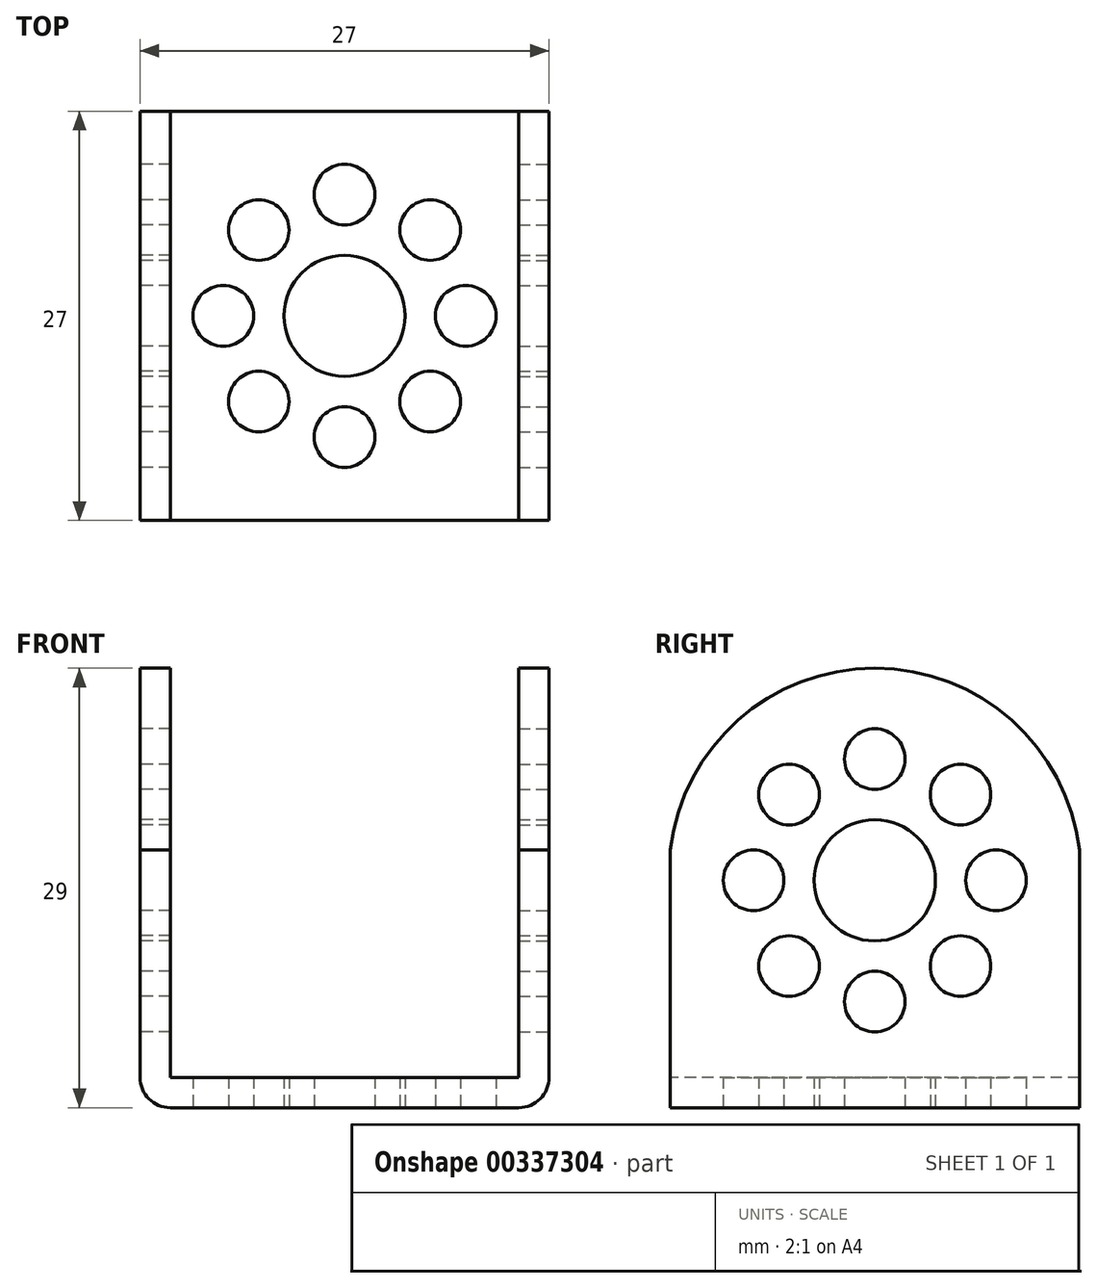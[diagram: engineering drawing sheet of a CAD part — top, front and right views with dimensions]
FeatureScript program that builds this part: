
annotation { "Feature Type Name" : "Feature", "Feature Type Description" : "" }
export const myFeature = defineFeature(function(context is Context, id is Id, definition is map)
    precondition{}
    {
        {
            var Q0;
            Q0=qCreatedBy(makeId("Top.planeOp"),FACE);
            var sketch = newSketch(context, id + "F0", { "sketchPlane" : qUnion([Q0])});
            skLineSegment(sketch, "E0.bottom", {"start": v(13.5, 13.5) * mm, "end": v(-13.5, 13.5) * mm});
            skLineSegment(sketch, "E0.top", {"start": v(13.5, -13.5) * mm, "end": v(-13.5, -13.5) * mm});
            skLineSegment(sketch, "E0.left", {"start": v(13.5, 13.5) * mm, "end": v(13.5, -13.5) * mm});
            skLineSegment(sketch, "E0.right", {"start": v(-13.5, 13.5) * mm, "end": v(-13.5, -13.5) * mm});
            skPoint(sketch, "E0.middle", {"position": v(0, 0) * mm});
            skLineSegment(sketch, "E1", {"start": v(0, 2.64) * mm, "end": v(0, 0) * mm});
            skLineSegment(sketch, "E2", {"start": v(0, 0) * mm, "end": v(0, -2.64) * mm});
            skLineSegment(sketch, "E3", {"start": v(-1.85, 0) * mm, "end": v(0, 0) * mm});
            skLineSegment(sketch, "E4", {"start": v(3.72, 0) * mm, "end": v(0, 0) * mm});
            skLineSegment(sketch, "E5", {"start": v(0, 0) * mm, "end": v(1.28, 1.28) * mm});
            skLineSegment(sketch, "E6", {"start": v(0, 0) * mm, "end": v(-1.4, -1.4) * mm});
            skLineSegment(sketch, "E7", {"start": v(0, 0) * mm, "end": v(-1.4, 1.4) * mm});
            skLineSegment(sketch, "E8", {"start": v(0, 0) * mm, "end": v(1.38, -1.38) * mm});
            skCircle(sketch, "E9", {"center": v(0, 0) * mm, "radius": 4 * mm});
            skCircle(sketch, "E10", {"center": v(-5.66, 5.66) * mm, "radius": 2 * mm});
            skCircle(sketch, "E11", {"center": v(0, 8) * mm, "radius": 2 * mm});
            skCircle(sketch, "E12", {"center": v(5.66, 5.66) * mm, "radius": 2 * mm});
            skCircle(sketch, "E13", {"center": v(8, 0) * mm, "radius": 2 * mm});
            skCircle(sketch, "E14", {"center": v(-8, 0) * mm, "radius": 2 * mm});
            skCircle(sketch, "E15", {"center": v(-5.66, -5.66) * mm, "radius": 2 * mm});
            skCircle(sketch, "E16", {"center": v(0, -8) * mm, "radius": 2 * mm});
            skCircle(sketch, "E17", {"center": v(5.66, -5.66) * mm, "radius": 2 * mm});
            skSolve(sketch);
        }
        {
            var Q0;
            Q0=sQuery(id+"F0.wireOp",EDGE,"E0.right");
            var Q1;
            Q1=qCreatedBy(makeId("Right.planeOp"),FACE);
            cPlane(context, id + "F1", {"entities" : qUnion([Q0, Q1]), "cplaneType" : CPlaneType.LINE_ANGLE, "offset" : 25.4 * mm, "angle" : 0 * degree, "width" : 152.4 * mm, "height" : 152.4 * mm});
        }
        {
            var Q0;
            Q0=sQuery(id+"F0.wireOp",EDGE,"E0.left");
            var Q1;
            Q1=qCreatedBy(makeId("Right.planeOp"),FACE);
            cPlane(context, id + "F2", {"entities" : qUnion([Q0, Q1]), "cplaneType" : CPlaneType.LINE_ANGLE, "offset" : 25.4 * mm, "angle" : 0 * degree, "width" : 152.4 * mm, "height" : 152.4 * mm});
        }
        {
            var Q0;
            Q0=qCreatedBy(id+"F1.planeOp",FACE);
            var sketch = newSketch(context, id + "F3", { "sketchPlane" : qUnion([Q0])});
            skLineSegment(sketch, "E18", {"start": v(-13.5, 0) * mm, "end": v(-13.5, 17) * mm});
            skLineSegment(sketch, "E19", {"start": v(-13.5, 0) * mm, "end": v(13.5, 0) * mm});
            skLineSegment(sketch, "E20", {"start": v(13.5, 0) * mm, "end": v(13.5, 17) * mm});
            skArc(sketch, "E21", {"start": v(13.5, 17) * mm, "mid": v(0, 29) * mm, "end": v(-13.5, 17) * mm});
            skLineSegment(sketch, "E22", {"start": v(0, 17.64) * mm, "end": v(0, 15) * mm});
            skLineSegment(sketch, "E23", {"start": v(0, 15) * mm, "end": v(0, 12.36) * mm});
            skLineSegment(sketch, "E24", {"start": v(-1.85, 15) * mm, "end": v(0, 15) * mm});
            skLineSegment(sketch, "E25", {"start": v(3.72, 15) * mm, "end": v(0, 15) * mm});
            skLineSegment(sketch, "E26", {"start": v(0, 15) * mm, "end": v(1.28, 16.28) * mm});
            skLineSegment(sketch, "E27", {"start": v(0, 15) * mm, "end": v(-1.4, 13.6) * mm});
            skLineSegment(sketch, "E28", {"start": v(0, 15) * mm, "end": v(-1.4, 16.4) * mm});
            skLineSegment(sketch, "E29", {"start": v(0, 15) * mm, "end": v(1.38, 13.62) * mm});
            skCircle(sketch, "E30", {"center": v(0, 15) * mm, "radius": 4 * mm});
            skCircle(sketch, "E31", {"center": v(-5.66, 20.66) * mm, "radius": 2 * mm});
            skCircle(sketch, "E32", {"center": v(0, 23) * mm, "radius": 2 * mm});
            skCircle(sketch, "E33", {"center": v(5.66, 20.66) * mm, "radius": 2 * mm});
            skCircle(sketch, "E34", {"center": v(8, 15) * mm, "radius": 2 * mm});
            skCircle(sketch, "E35", {"center": v(-8, 15) * mm, "radius": 2 * mm});
            skCircle(sketch, "E36", {"center": v(-5.66, 9.34) * mm, "radius": 2 * mm});
            skCircle(sketch, "E37", {"center": v(0, 7) * mm, "radius": 2 * mm});
            skCircle(sketch, "E38", {"center": v(5.66, 9.34) * mm, "radius": 2 * mm});
            skSolve(sketch);
        }
        {
            var Q0;
            Q0=qCreatedBy(id+"F2.planeOp",FACE);
            var sketch = newSketch(context, id + "F4", { "sketchPlane" : qUnion([Q0])});
            skLineSegment(sketch, "E39", {"start": v(13.5, 0) * mm, "end": v(13.5, 17) * mm});
            skLineSegment(sketch, "E40", {"start": v(-13.5, 0) * mm, "end": v(-13.5, 17) * mm});
            skArc(sketch, "E41", {"start": v(13.5, 17) * mm, "mid": v(0, 29) * mm, "end": v(-13.5, 17) * mm});
            skLineSegment(sketch, "E42", {"start": v(0, 15) * mm, "end": v(0, 13.5) * mm});
            skLineSegment(sketch, "E43", {"start": v(0, 15) * mm, "end": v(0, 8.22) * mm});
            skLineSegment(sketch, "E44", {"start": v(-1.85, 15) * mm, "end": v(0, 15) * mm});
            skLineSegment(sketch, "E45", {"start": v(3.72, 15) * mm, "end": v(0, 15) * mm});
            skLineSegment(sketch, "E46", {"start": v(0, 15) * mm, "end": v(1.28, 16.28) * mm});
            skLineSegment(sketch, "E47", {"start": v(0, 15) * mm, "end": v(-1.4, 13.6) * mm});
            skLineSegment(sketch, "E48", {"start": v(0, 15) * mm, "end": v(-1.4, 16.4) * mm});
            skLineSegment(sketch, "E49", {"start": v(0, 15) * mm, "end": v(1.38, 13.62) * mm});
            skCircle(sketch, "E50", {"center": v(0, 15) * mm, "radius": 4 * mm});
            skCircle(sketch, "E51", {"center": v(-5.66, 20.66) * mm, "radius": 2 * mm});
            skCircle(sketch, "E52", {"center": v(0, 23) * mm, "radius": 2 * mm});
            skCircle(sketch, "E53", {"center": v(5.66, 20.66) * mm, "radius": 2 * mm});
            skCircle(sketch, "E54", {"center": v(8, 15) * mm, "radius": 2 * mm});
            skCircle(sketch, "E55", {"center": v(-8, 15) * mm, "radius": 2 * mm});
            skCircle(sketch, "E56", {"center": v(-5.66, 9.34) * mm, "radius": 2 * mm});
            skCircle(sketch, "E57", {"center": v(0, 7) * mm, "radius": 2 * mm});
            skCircle(sketch, "E58", {"center": v(5.66, 9.34) * mm, "radius": 2 * mm});
            skLineSegment(sketch, "E59", {"start": v(13.5, 0) * mm, "end": v(-13.5, 0) * mm});
            skSolve(sketch);
        }
        {
            var Q0;
            Q0=makeQuery(id+"F0.imprint","IMPRINT",FACE,{"disambiguationData":[TD([[makeQuery(id+"F0.imprint","IMPRINT",EDGE,{"derivedFrom":sQuery(id+"F0.wireOp",EDGE,"E0.bottom")}),1.0]])]});
            extrude(context, id + "F5", {"entities" : qUnion([Q0]), "depth" : 2 * mm});
        }
        {
            var Q0;
            Q0=makeQuery(id+"F3.imprint","IMPRINT",FACE,{"disambiguationData":[TD([[makeQuery(id+"F3.imprint","IMPRINT",EDGE,{"derivedFrom":sQuery(id+"F3.wireOp",EDGE,"E18")}),-1.0]])]});
            extrude(context, id + "F6", {"entities" : qUnion([Q0]), "operationType" : NewBodyOperationType.ADD, "oppositeDirection" : true, "depth" : 2 * mm});
        }
        {
            var Q0;
            Q0=makeQuery(id+"F4.imprint","IMPRINT",FACE,{"disambiguationData":[TD([[makeQuery(id+"F4.imprint","IMPRINT",EDGE,{"derivedFrom":sQuery(id+"F4.wireOp",EDGE,"E39")}),1.0]])]});
            extrude(context, id + "F7", {"entities" : qUnion([Q0]), "operationType" : NewBodyOperationType.ADD, "depth" : 2 * mm});
        }
        {
            var Q0;
            Q0=makeQuery(id+"F5.opExtrude","CAP_EDGE",EDGE,{"disambiguationData":[OSD([sQuery(id+"F0.wireOp",EDGE,"E0.right")])],"isStart":true});
            fillet(context, id + "F8", {"entities" : qUnion([Q0]), "radius" : 2 * mm, "tangentPropagation" : true, "allowEdgeOverflow" : false});
        }
        {
            var Q0;
            Q0=makeQuery(id+"F5.opExtrude","CAP_EDGE",EDGE,{"disambiguationData":[OSD([sQuery(id+"F0.wireOp",EDGE,"E0.left")])],"isStart":true});
            fillet(context, id + "F9", {"entities" : qUnion([Q0]), "radius" : 2 * mm, "tangentPropagation" : true, "allowEdgeOverflow" : false});
        }
    });
